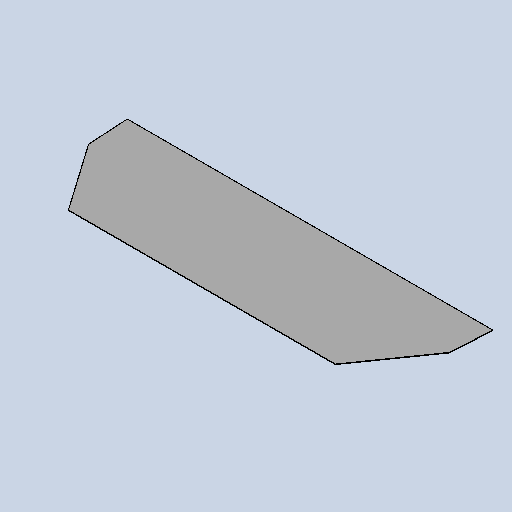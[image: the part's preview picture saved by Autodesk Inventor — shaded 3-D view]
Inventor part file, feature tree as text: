
AUTODESK INVENTOR PART (.ipt)
format: ipt  version: 2025 (Build 290162010, 162A)  size: 122,368 bytes
history: native  units: mm
features: sketch x2, other x2, sheet_metal_op x1, extrude x1, mirror x1, projected_geometry x1
ambient origin geometry x8: Origin, YZ Plane, XZ Plane, XY Plane, X Axis, Y Axis, Z Axis, Center Point
bodies: Solid1 (feature_tree)
feature tree (8):
  sheet_metal_op  "Face1"
  extrude  "Extrusion1"  Depth=450.0mm
  mirror  "Mirror1"
  sketch  "Sketch1"  dims[d0=450.0mm d1=1520.0mm]
  other  "Plate1"
  sketch  "Sketch2"  dims[d2=2.0mm d3=0.1mm d8=10.0mm d9=171.0mm d10=205.0mm d11=0.0mm d12=0.0mm]
  projected_geometry  "Projected Loop1"
  other  "Definition1"
